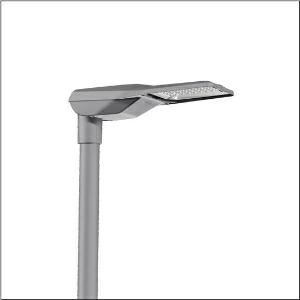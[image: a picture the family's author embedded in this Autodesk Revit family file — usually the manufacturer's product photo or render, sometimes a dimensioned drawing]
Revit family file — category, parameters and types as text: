
# Revit family: streetlight_sl_21_iq_mini___st0_8a_5xe2c61g08hb_b958
name_source: partatom
category: Lighting Fixtures
units: mm (PartAtom-declared; Revit-internal decimal feet)

## family parameters
Cut with Voids When Loaded = No
Host = Face
Light Source = No
Part Type = Normal
Room Calculation Point = No
Round Connector Dimension = Use Diameter
Shared = No

## types (1)
- --- (1 x LED, 8480 lm, 70.9 W, 2700K)
    Apparent Load = 71 VA
    CIE Flux Codes = 38 75 97 100 100
    Color Rendering = 70
    Color Temperature = 2700K
    Default Elevation = 1800 mm
    Description = Streetlight SL 21 iQ mini, mast luminaire, primary light control with lens, of PMMA, primary optical cover: cover, of toughened safety glass, transparent, light distribution: ST0.8a, light emission: direct distribution, primary light characteristic: asymmetric, installation type: post-top, side-entry, LED, High Power LED, rated luminous flux: 8.480lm, luminous efficacy: 120lm/W, light colour: 727, colour temperature: 2700K, control: Street-Remote, Auto-Match, Temp-Guard, Lumen-Switch, Night-Set, Smart-Wire, Light-Fading, Desk-Remote (wireless, voltage-free reading and setting of iQ features in the workshop via application-optimized NFC function/RFID function), optimised constant luminous flux control (CLO 2.0), presetting dimming linear, mains connection: 220..240V, AC, 50/60Hz, start of lifetime: 71W, end of service life: 75W, reduction: 31W, luminaire housing, of diecast aluminium, powder-coated, Siteco® metallic grey (DB 702S), corrosivity category C5 mid according to DIN EN ISO 12944, please order mast flange separately, inclination adjustable: 0°, 5°, 10°, 15°, sealing non-destructively replaceable, multi-level sealing system, length: 628mm, width: 235mm, height: 110mm, mast flange for spigot size: 42mm (side-entry): 5XC10008XM4, 60/48mm (side-entry/post-top): 5XC10108XM2, 76/60mm (side-entry/post-top): 5XC10108XM1, protection rating (complete): IP66, insulation class (complete): insulation class II (safety insulation), certification: CE, ENEC, ENEC+, VDE, impact resistance: IK09, permissible operating ambient temperature for outdoor applications: -40..+50°C, standard-compliant lighting for roads and squares, packaging unit: 1 piece

Light Distribution: ST0.8a
    Height = 110 mm
    Lamp = 1 x LED
    Lamp Light Flux = 8480 lm
    Lamp Power = 70.9 W
    Lamp count = 1
    Length = 625 mm
    Luminous efficacy = 120 lm/W
    Manufacturer = Siteco
    ModVariant = No
    Model = 5XE2C61G08HB
    Number of Poles = 1
    OnlyDefault = Yes
    Power Factor = 1
    Product Name = Streetlight SL 21 iQ mini | ST0.8a
    Product group = mast luminaire | pylon top
    ProductGroupID = 6100
    Protection Class = Protection class II
    Protection Degree = IP 66
    RLX_Detail_Level = 1
    RLX_Emergency_Light_Flux = 0 lm
    RLX_Emergency_Type = 0
    RLX_Emergency_Type_DB = No
    RlxData = <blob elided: 92441 chars, md5=ed240e0c>
    Socket = socket
    Standby Power = 0 W
    System Light Flux = 8480 lm
    System Power = 71 W
    Type Comments = factory setting: luminous flux: 100 % | dim-lin: 254 | 711 mA
    Type Image = l_1003519.jpg
    URL = http://relux.com
    VarID = @adj_089811
    Voltage = 0 V
    Weight = 0.00 kg
    Width = 234 mm

## geometry (parser evidence)
native form markers: Blend x4, Sweep x11
no freeform markers — native parametric forms only
